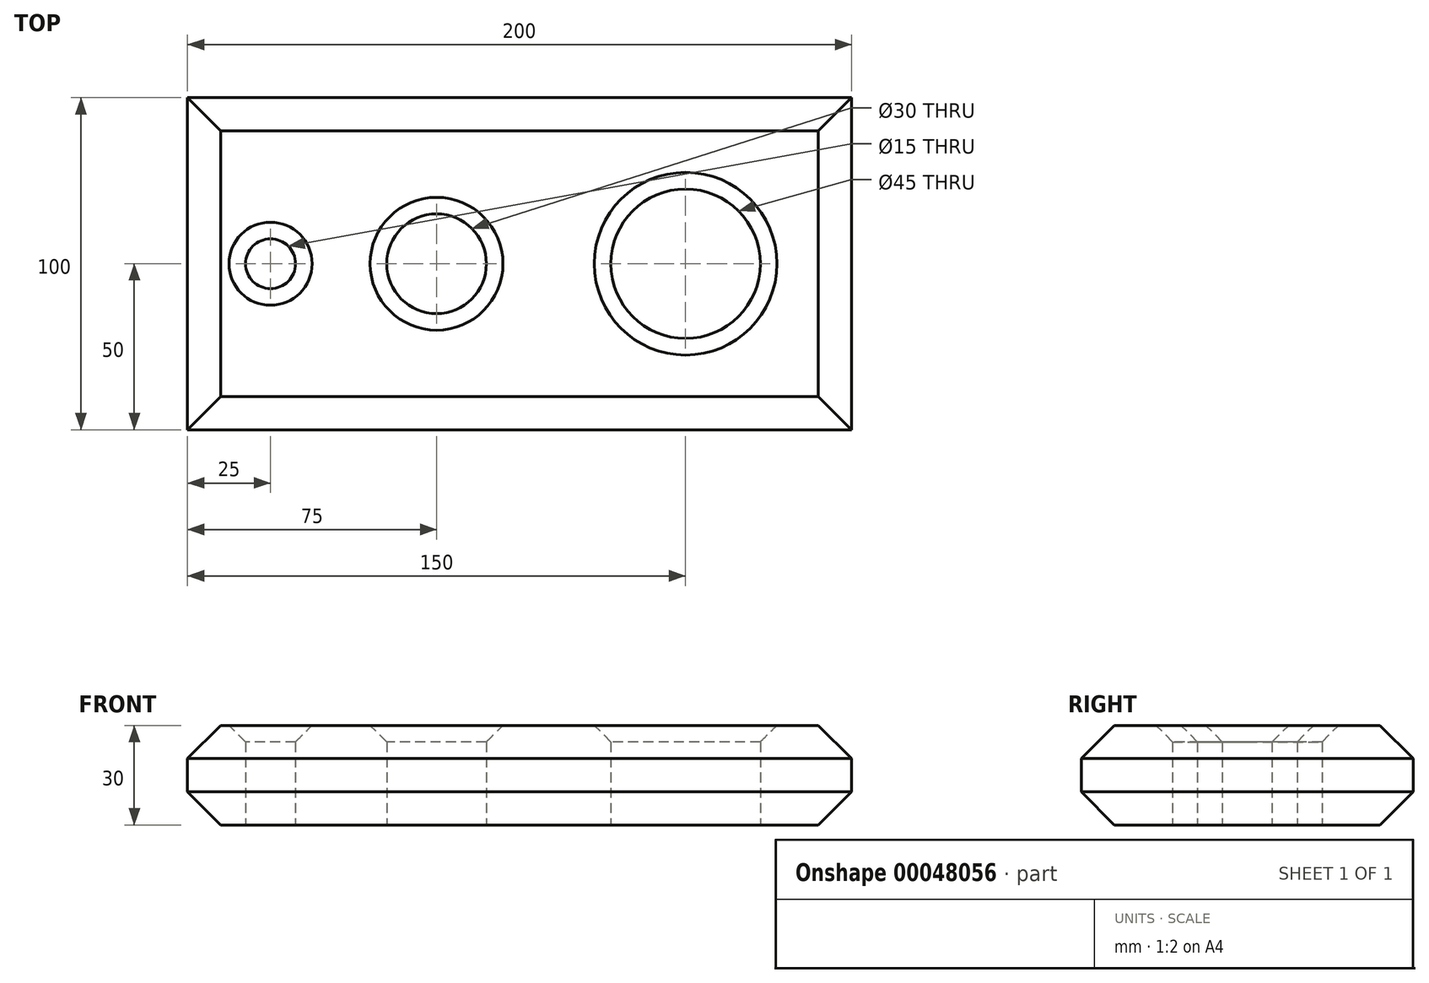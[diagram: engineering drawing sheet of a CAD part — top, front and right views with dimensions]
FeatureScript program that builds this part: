
annotation { "Feature Type Name" : "Feature", "Feature Type Description" : "" }
export const myFeature = defineFeature(function(context is Context, id is Id, definition is map)
    precondition{}
    {
        {
            var Q0;
            Q0=qCreatedBy(makeId("Top.planeOp"),FACE);
            var sketch = newSketch(context, id + "F0", { "sketchPlane" : qUnion([Q0])});
            skLineSegment(sketch, "E0.bottom", {"start": v(0, 0) * mm, "end": v(200, 0) * mm});
            skLineSegment(sketch, "E0.top", {"start": v(0, 100) * mm, "end": v(200, 100) * mm});
            skLineSegment(sketch, "E0.left", {"start": v(0, 0) * mm, "end": v(0, 100) * mm});
            skLineSegment(sketch, "E0.right", {"start": v(200, 0) * mm, "end": v(200, 100) * mm});
            skCircle(sketch, "E1", {"center": v(25, 50) * mm, "radius": 7.5 * mm});
            skCircle(sketch, "E2", {"center": v(75, 50) * mm, "radius": 15 * mm});
            skCircle(sketch, "E3", {"center": v(150, 50) * mm, "radius": 22.5 * mm});
            skLineSegment(sketch, "E4", {"start": v(0, 50) * mm, "end": v(200, 50) * mm, "construction": true});
            skSolve(sketch);
        }
        {
            var Q0;
            Q0=makeQuery(id+"F0.imprint","IMPRINT",FACE,{"disambiguationData":[TD([[makeQuery(id+"F0.imprint","IMPRINT",EDGE,{"derivedFrom":sQuery(id+"F0.wireOp",EDGE,"E0.bottom")}),1.0]])]});
            extrude(context, id + "F1", {"entities" : qUnion([Q0]), "depth" : 30 * mm});
        }
        {
            var Q0;
            Q0=makeQuery(id+"F1.opExtrude","CAP_EDGE",EDGE,{"disambiguationData":[OSD([sQuery(id+"F0.wireOp",EDGE,"E0.left")])],"isStart":false});
            var Q1;
            Q1=makeQuery(id+"F1.opExtrude","CAP_EDGE",EDGE,{"disambiguationData":[OSD([sQuery(id+"F0.wireOp",EDGE,"E0.top")])],"isStart":false});
            var Q2;
            Q2=makeQuery(id+"F1.opExtrude","CAP_EDGE",EDGE,{"disambiguationData":[OSD([sQuery(id+"F0.wireOp",EDGE,"E0.bottom")])],"isStart":false});
            var Q3;
            Q3=makeQuery(id+"F1.opExtrude","CAP_EDGE",EDGE,{"disambiguationData":[OSD([sQuery(id+"F0.wireOp",EDGE,"E0.right")])],"isStart":false});
            var Q4;
            Q4=makeQuery(id+"F1.opExtrude","CAP_EDGE",EDGE,{"disambiguationData":[OSD([sQuery(id+"F0.wireOp",EDGE,"E0.right")])],"isStart":true});
            var Q5;
            Q5=makeQuery(id+"F1.opExtrude","CAP_EDGE",EDGE,{"disambiguationData":[OSD([sQuery(id+"F0.wireOp",EDGE,"E0.top")])],"isStart":true});
            var Q6;
            Q6=makeQuery(id+"F1.opExtrude","CAP_EDGE",EDGE,{"disambiguationData":[OSD([sQuery(id+"F0.wireOp",EDGE,"E0.left")])],"isStart":true});
            var Q7;
            Q7=makeQuery(id+"F1.opExtrude","CAP_EDGE",EDGE,{"disambiguationData":[OSD([sQuery(id+"F0.wireOp",EDGE,"E0.bottom")])],"isStart":true});
            chamfer(context, id + "F2", {"entities" : qUnion([Q0, Q1, Q2, Q3, Q4, Q5, Q6, Q7]), "chamferType" : ChamferType.OFFSET_ANGLE, "width" : 10 * mm, "oppositeDirection" : false, "angle" : 45 * degree, "tangentPropagation" : true});
        }
        {
            var Q0;
            Q0=makeQuery(id+"F1.opExtrude","CAP_EDGE",EDGE,{"disambiguationData":[OSD([sQuery(id+"F0.wireOp",EDGE,"E3")])],"isStart":false});
            var Q1;
            Q1=makeQuery(id+"F1.opExtrude","CAP_EDGE",EDGE,{"disambiguationData":[OSD([sQuery(id+"F0.wireOp",EDGE,"E2")])],"isStart":false});
            var Q2;
            Q2=makeQuery(id+"F1.opExtrude","CAP_EDGE",EDGE,{"disambiguationData":[OSD([sQuery(id+"F0.wireOp",EDGE,"E1")])],"isStart":false});
            chamfer(context, id + "F3", {"entities" : qUnion([Q0, Q1, Q2]), "chamferType" : ChamferType.OFFSET_ANGLE, "width" : 5 * mm, "oppositeDirection" : false, "angle" : 45 * degree, "tangentPropagation" : true});
        }
    });
